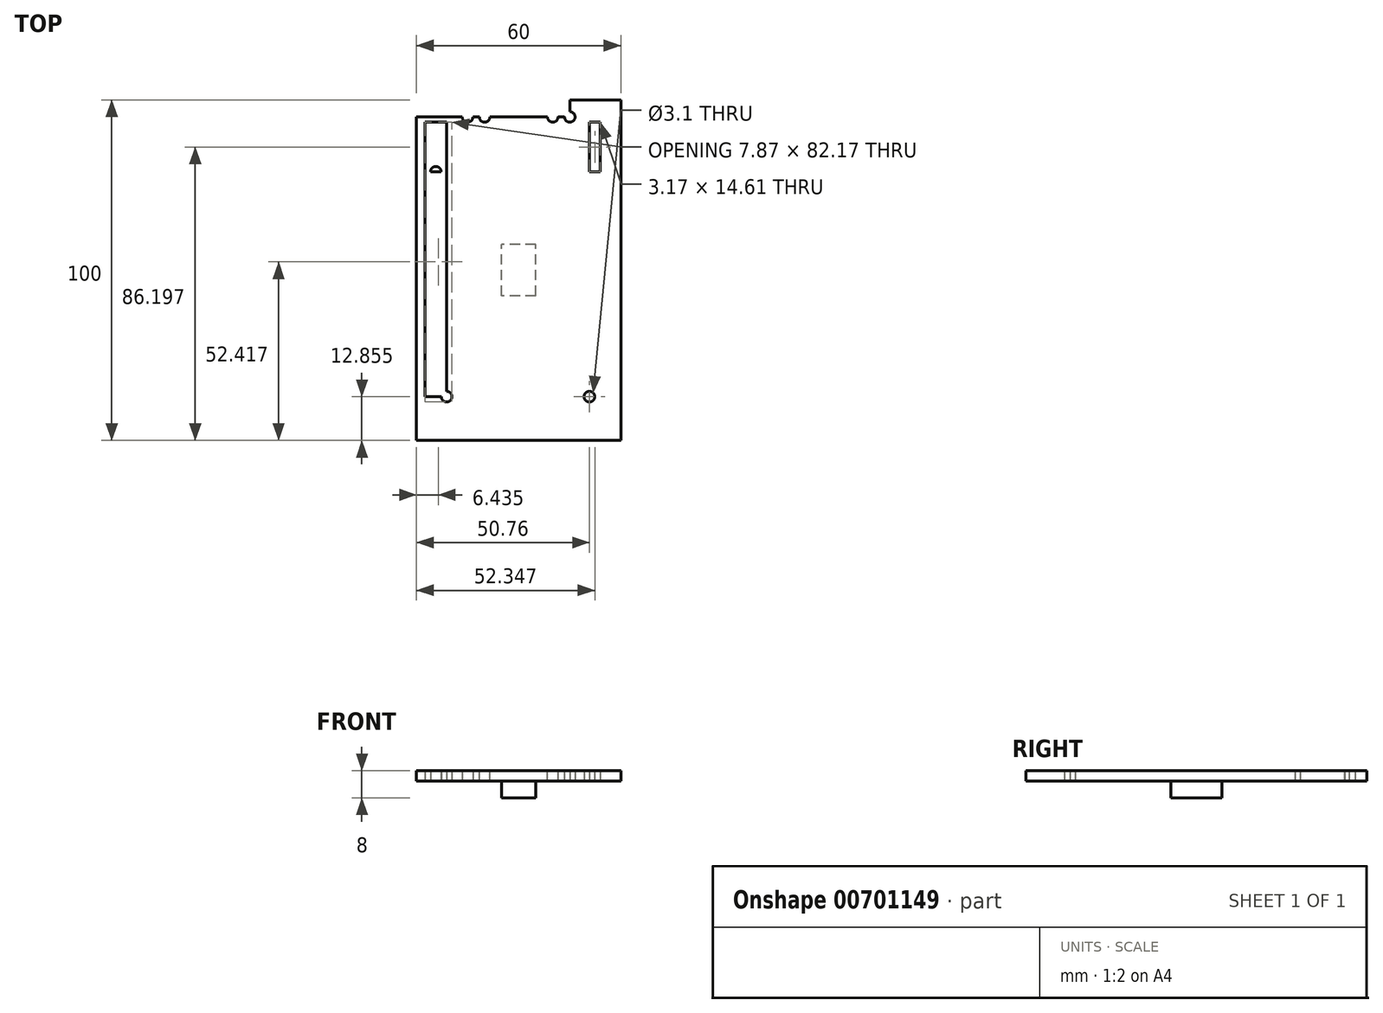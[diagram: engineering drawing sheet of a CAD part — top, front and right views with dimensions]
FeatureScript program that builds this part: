
annotation { "Feature Type Name" : "Feature", "Feature Type Description" : "" }
export const myFeature = defineFeature(function(context is Context, id is Id, definition is map)
    precondition{}
    {
        {
            var Q0;
            Q0=qCreatedBy(makeId("Top.planeOp"),FACE);
            var sketch = newSketch(context, id + "F0", { "sketchPlane" : qUnion([Q0])});
            skLineSegment(sketch, "E0.bottom", {"start": v(30, -50) * mm, "end": v(-30, -50) * mm});
            skLineSegment(sketch, "E0.top", {"start": v(30, 50) * mm, "end": v(-30, 50) * mm});
            skLineSegment(sketch, "E0.left", {"start": v(30, -50) * mm, "end": v(30, 50) * mm});
            skLineSegment(sketch, "E0.right", {"start": v(-30, -50) * mm, "end": v(-30, 50) * mm});
            skPoint(sketch, "E0.middle", {"position": v(0, 0) * mm});
            skLineSegment(sketch, "E1.bottom", {"start": v(-30, 50) * mm, "end": v(-15, 50) * mm});
            skLineSegment(sketch, "E1.top", {"start": v(-30, 45) * mm, "end": v(-15, 45) * mm});
            skLineSegment(sketch, "E1.left", {"start": v(-30, 50) * mm, "end": v(-30, 45) * mm});
            skLineSegment(sketch, "E1.right", {"start": v(-15, 50) * mm, "end": v(-15, 45) * mm});
            skLineSegment(sketch, "E2.bottom", {"start": v(-15, 50) * mm, "end": v(15, 50) * mm});
            skLineSegment(sketch, "E2.top", {"start": v(-15, 45) * mm, "end": v(15, 45) * mm});
            skLineSegment(sketch, "E2.right", {"start": v(15, 50) * mm, "end": v(15, 45) * mm});
            skCircle(sketch, "E3", {"center": v(-15, 45) * mm, "radius": 1.55 * mm});
            skCircle(sketch, "E4", {"center": v(15, 45) * mm, "radius": 1.55 * mm});
            skLineSegment(sketch, "E5.bottom", {"start": v(5, -7.5) * mm, "end": v(-5, -7.5) * mm});
            skLineSegment(sketch, "E5.top", {"start": v(5, 7.5) * mm, "end": v(-5, 7.5) * mm});
            skLineSegment(sketch, "E5.left", {"start": v(5, -7.5) * mm, "end": v(5, 7.5) * mm});
            skLineSegment(sketch, "E5.right", {"start": v(-5, -7.5) * mm, "end": v(-5, 7.5) * mm});
            skLineSegment(sketch, "E6.bottom", {"start": v(27.5, -43.5) * mm, "end": v(-27.5, -43.5) * mm});
            skLineSegment(sketch, "E6.top", {"start": v(27.5, 43.5) * mm, "end": v(-27.5, 43.5) * mm});
            skLineSegment(sketch, "E6.left", {"start": v(27.5, -43.5) * mm, "end": v(27.5, 43.5) * mm});
            skLineSegment(sketch, "E6.right", {"start": v(-27.5, -43.5) * mm, "end": v(-27.5, 43.5) * mm});
            skLineSegment(sketch, "E7.bottom", {"start": v(-27.5, 43.5) * mm, "end": v(-24.33, 43.5) * mm});
            skLineSegment(sketch, "E7.top", {"start": v(-27.5, 28.9) * mm, "end": v(-24.33, 28.9) * mm});
            skLineSegment(sketch, "E7.left", {"start": v(-27.5, 43.5) * mm, "end": v(-27.5, 28.9) * mm});
            skLineSegment(sketch, "E7.right", {"start": v(-24.33, 43.5) * mm, "end": v(-24.33, 28.9) * mm});
            skLineSegment(sketch, "E8.bottom", {"start": v(-27.5, 43.5) * mm, "end": v(23.93, 43.5) * mm});
            skLineSegment(sketch, "E8.top", {"start": v(-27.5, 28.9) * mm, "end": v(23.93, 28.9) * mm});
            skLineSegment(sketch, "E8.right", {"start": v(23.93, 43.5) * mm, "end": v(23.93, 28.9) * mm});
            skCircle(sketch, "E9", {"center": v(-24.33, 28.9) * mm, "radius": 1.55 * mm});
            skCircle(sketch, "E10", {"center": v(23.93, 28.9) * mm, "radius": 1.55 * mm});
            skLineSegment(sketch, "E11.bottom", {"start": v(-27.5, 43.5) * mm, "end": v(-21.15, 43.5) * mm});
            skLineSegment(sketch, "E11.top", {"start": v(-27.5, -37.14) * mm, "end": v(-21.15, -37.14) * mm});
            skLineSegment(sketch, "E11.left", {"start": v(-27.5, 43.5) * mm, "end": v(-27.5, -37.14) * mm});
            skLineSegment(sketch, "E11.right", {"start": v(-21.15, 43.5) * mm, "end": v(-21.15, -37.15) * mm});
            skLineSegment(sketch, "E12.bottom", {"start": v(-27.5, 43.5) * mm, "end": v(20.76, 43.5) * mm});
            skLineSegment(sketch, "E12.top", {"start": v(-27.5, -37.14) * mm, "end": v(20.76, -37.14) * mm});
            skLineSegment(sketch, "E12.right", {"start": v(20.76, 43.5) * mm, "end": v(20.76, -37.14) * mm});
            skCircle(sketch, "E13", {"center": v(-21.15, -37.14) * mm, "radius": 1.55 * mm});
            skCircle(sketch, "E14", {"center": v(20.76, -37.14) * mm, "radius": 1.55 * mm});
            skSolve(sketch);
        }
        {
            var Q0;
            Q0=makeQuery(id+"F0.imprint","IMPRINT",FACE,{"disambiguationData":[TD([[makeQuery(id+"F0.imprint","IMPRINT",EDGE,{"derivedFrom":sQuery(id+"F0.wireOp",EDGE,"E5.bottom")}),-1.0]])]});
            extrude(context, id + "F1", {"entities" : qUnion([Q0]), "oppositeDirection" : true, "depth" : 5 * mm, "offsetDistance" : 25 * mm});
        }
        {
            var Q0;
            Q0=makeQuery(id+"F0.imprint","IMPRINT",FACE,{"disambiguationData":[TD([[makeQuery(id+"F0.imprint","IMPRINT",EDGE,{"derivedFrom":sQuery(id+"F0.wireOp",EDGE,"E5.bottom")}),1.0]])]});
            var Q1;
            Q1=makeQuery(id+"F0.imprint","IMPRINT",FACE,{"disambiguationData":[TD([[makeQuery(id+"F0.imprint","IMPRINT",EDGE,{"derivedFrom":sQuery(id+"F0.wireOp",EDGE,"E5.bottom")}),-1.0]])]});
            var Q2;
            {var subQ1=sQuery(id+"F0.wireOp",EDGE,"E8.top");var subQ4=sQuery(id+"F0.wireOp",EDGE,"E11.left");var subQ5=makeQuery(id+"F0.imprint","INTERSECT",VERTEX,{"derivedFrom":[subQ1,subQ4]});Q2=makeQuery(id+"F0.imprint","IMPRINT",FACE,{"disambiguationData":[TD([[makeQuery(id+"F0.imprint","IMPRINT",EDGE,{"disambiguationData":[TD([[subQ5,-1.0]])],"derivedFrom":subQ1}),-1.0]])]});}
            var Q3;
            Q3=makeQuery(id+"F0.imprint","IMPRINT",FACE,{"disambiguationData":[TD([[makeQuery(id+"F0.imprint","IMPRINT",EDGE,{"derivedFrom":sQuery(id+"F0.wireOp",EDGE,"E0.bottom")}),-1.0]])]});
            var Q4;
            Q4=makeQuery(id+"F0.imprint","IMPRINT",FACE,{"disambiguationData":[TD([[makeQuery(id+"F0.imprint","IMPRINT",EDGE,{"derivedFrom":sQuery(id+"F0.wireOp",EDGE,"E6.bottom")}),-1.0]])]});
            var Q5;
            {var subQ1=sQuery(id+"F0.wireOp",EDGE,"E7.right");var subQ7=sQuery(id+"F0.wireOp",EDGE,"E12.bottom");var subQ8=makeQuery(id+"F0.imprint","INTERSECT",VERTEX,{"derivedFrom":[subQ1,subQ7]});Q5=makeQuery(id+"F0.imprint","IMPRINT",FACE,{"disambiguationData":[TD([[makeQuery(id+"F0.imprint","IMPRINT",EDGE,{"disambiguationData":[TD([[subQ8,-1.0]])],"derivedFrom":subQ1}),-1.0]])]});}
            var Q6;
            {var subQ0=sQuery(id+"F0.wireOp",EDGE,"E12.bottom");var subQ7=sQuery(id+"F0.wireOp",EDGE,"E7.right");var subQ9=makeQuery(id+"F0.imprint","INTERSECT",VERTEX,{"derivedFrom":[subQ7,subQ0]});Q6=makeQuery(id+"F0.imprint","IMPRINT",FACE,{"disambiguationData":[TD([[makeQuery(id+"F0.imprint","IMPRINT",EDGE,{"disambiguationData":[TD([[subQ9,-1.0]])],"derivedFrom":subQ7}),1.0]])]});}
            var Q7;
            {var subQ0=sQuery(id+"F0.wireOp",EDGE,"E12.bottom");var subQ11=sQuery(id+"F0.wireOp",EDGE,"E3");var subQ12=makeQuery(id+"F0.imprint","INTERSECT",VERTEX,{"disambiguationData":[OD(0.0)],"derivedFrom":[subQ11,subQ0]});Q7=makeQuery(id+"F0.imprint","IMPRINT",FACE,{"disambiguationData":[TD([[makeQuery(id+"F0.imprint","IMPRINT",EDGE,{"disambiguationData":[TD([[subQ12,-1.0]])],"derivedFrom":subQ11}),-1.0]])]});}
            var Q8;
            {var subQ5=sQuery(id+"F0.wireOp",EDGE,"E8.bottom");Q8=makeQuery(id+"F0.imprint","IMPRINT",FACE,{"disambiguationData":[TD([[makeQuery(id+"F0.imprint","IMPRINT",EDGE,{"derivedFrom":subQ5}),-1.0]])]});}
            var Q9;
            {var subQ1=sQuery(id+"F0.wireOp",EDGE,"E2.bottom");Q9=makeQuery(id+"F0.imprint","IMPRINT",FACE,{"disambiguationData":[TD([[makeQuery(id+"F0.imprint","IMPRINT",EDGE,{"derivedFrom":subQ1}),-1.0]])]});}
            var Q10;
            {var subQ1=sQuery(id+"F0.wireOp",EDGE,"E1.bottom");Q10=makeQuery(id+"F0.imprint","IMPRINT",FACE,{"disambiguationData":[TD([[makeQuery(id+"F0.imprint","IMPRINT",EDGE,{"derivedFrom":subQ1}),-1.0]])]});}
            var Q11;
            {var subQ0=sQuery(id+"F0.wireOp",EDGE,"E3");var subQ1=sQuery(id+"F0.wireOp",EDGE,"E2.top");var subQ2=makeQuery(id+"F0.imprint","INTERSECT",VERTEX,{"derivedFrom":[subQ1,subQ0]});Q11=makeQuery(id+"F0.imprint","IMPRINT",FACE,{"disambiguationData":[TD([[makeQuery(id+"F0.imprint","IMPRINT",EDGE,{"disambiguationData":[TD([[subQ2,-1.0]])],"derivedFrom":subQ1}),-1.0]])]});}
            extrude(context, id + "F2", {"entities" : qUnion([Q0, Q1, Q2, Q3, Q4, Q5, Q6, Q7, Q8, Q9, Q10, Q11]), "operationType" : NewBodyOperationType.ADD, "depth" : 3 * mm, "offsetDistance" : 25 * mm});
        }
        {
            var Q0;
            Q0=makeQuery(id+"F2.opExtrude","CAP_FACE",FACE,{"disambiguationData":[OSD([sQuery(id+"F0.wireOp",EDGE,"E0.bottom"),sQuery(id+"F0.wireOp",EDGE,"E0.top"),sQuery(id+"F0.wireOp",EDGE,"E0.left"),sQuery(id+"F0.wireOp",EDGE,"E0.right"),sQuery(id+"F0.wireOp",EDGE,"E1.bottom"),sQuery(id+"F0.wireOp",EDGE,"E1.left"),sQuery(id+"F0.wireOp",EDGE,"E2.bottom"),sQuery(id+"F0.wireOp",EDGE,"E3"),sQuery(id+"F0.wireOp",EDGE,"E4"),sQuery(id+"F0.wireOp",EDGE,"E9"),sQuery(id+"F0.wireOp",EDGE,"E10"),sQuery(id+"F0.wireOp",EDGE,"E13"),sQuery(id+"F0.wireOp",EDGE,"E14")])],"isStart":false});
            var sketch = newSketch(context, id + "F3", { "sketchPlane" : qUnion([Q0])});
            skLineSegment(sketch, "E15.bottom", {"start": v(-30, 50) * mm, "end": v(30, 50) * mm});
            skLineSegment(sketch, "E15.top", {"start": v(-30, 45) * mm, "end": v(30, 45) * mm});
            skLineSegment(sketch, "E15.left", {"start": v(-30, 50) * mm, "end": v(-30, 45) * mm});
            skLineSegment(sketch, "E15.right", {"start": v(30, 50) * mm, "end": v(30, 45) * mm});
            skLineSegment(sketch, "E16.top", {"start": v(-30, 40) * mm, "end": v(30, 40) * mm});
            skLineSegment(sketch, "E16.left", {"start": v(-30, 45) * mm, "end": v(-30, 40) * mm});
            skLineSegment(sketch, "E16.right", {"start": v(30, 45) * mm, "end": v(30, 40) * mm});
            skLineSegment(sketch, "E17.bottom", {"start": v(-30, 50) * mm, "end": v(-10, 50) * mm});
            skLineSegment(sketch, "E17.top", {"start": v(-30, 45) * mm, "end": v(-10, 45) * mm});
            skLineSegment(sketch, "E17.right", {"start": v(-10, 50) * mm, "end": v(-10, 45) * mm});
            skLineSegment(sketch, "E18.bottom", {"start": v(30, 50) * mm, "end": v(10, 50) * mm});
            skLineSegment(sketch, "E18.top", {"start": v(30, 45) * mm, "end": v(10, 45) * mm});
            skLineSegment(sketch, "E18.right", {"start": v(10, 50) * mm, "end": v(10, 45) * mm});
            skCircle(sketch, "E19", {"center": v(-10, 45) * mm, "radius": 1.55 * mm});
            skCircle(sketch, "E20", {"center": v(10, 45) * mm, "radius": 1.55 * mm});
            skSolve(sketch);
        }
        {
            var Q0;
            {var subQ1=sQuery(id+"F3.wireOp",EDGE,"E15.bottom");Q0=makeQuery(id+"F3.imprint","IMPRINT",FACE,{"disambiguationData":[TD([[makeQuery(id+"F3.imprint","IMPRINT",EDGE,{"derivedFrom":subQ1}),1.0]])]});}
            var Q1;
            {var subQ7=sQuery(id+"F3.wireOp",EDGE,"E18.bottom");Q1=makeQuery(id+"F3.imprint","IMPRINT",FACE,{"disambiguationData":[TD([[makeQuery(id+"F3.imprint","IMPRINT",EDGE,{"derivedFrom":subQ7}),1.0]])]});}
            var Q2;
            Q2=makeQuery(id+"F3.imprint","IMPRINT",FACE,{"disambiguationData":[TD([[makeQuery(id+"F3.imprint","IMPRINT",EDGE,{"derivedFrom":sQuery(id+"F3.wireOp",EDGE,"E16.top")}),1.0]])]});
            var Q3;
            {var subQ0=sQuery(id+"F3.wireOp",EDGE,"E17.top");var subQ1=makeQuery(id+"F2.opExtrude","CAP_EDGE",EDGE,{"disambiguationData":[OSD([sQuery(id+"F0.wireOp",EDGE,"E3")])],"isStart":false});var subQ2=makeQuery(id+"F3.imprint","INTERSECT",VERTEX,{"disambiguationData":[OD(0.0)],"derivedFrom":[subQ1,subQ0]});Q3=makeQuery(id+"F3.imprint","IMPRINT",FACE,{"disambiguationData":[TD([[makeQuery(id+"F3.imprint","IMPRINT",EDGE,{"disambiguationData":[TD([[subQ2,-1.0]])],"derivedFrom":subQ0}),-1.0]])]});}
            var Q4;
            {var subQ0=sQuery(id+"F3.wireOp",EDGE,"E17.top");var subQ1=makeQuery(id+"F2.opExtrude","CAP_EDGE",EDGE,{"disambiguationData":[OSD([sQuery(id+"F0.wireOp",EDGE,"E3")])],"isStart":false});var subQ2=makeQuery(id+"F3.imprint","INTERSECT",VERTEX,{"disambiguationData":[OD(0.0)],"derivedFrom":[subQ1,subQ0]});Q4=makeQuery(id+"F3.imprint","IMPRINT",FACE,{"disambiguationData":[TD([[makeQuery(id+"F3.imprint","IMPRINT",EDGE,{"disambiguationData":[TD([[subQ2,-1.0]])],"derivedFrom":subQ0}),1.0]])]});}
            var Q5;
            {var subQ7=sQuery(id+"F3.wireOp",EDGE,"E17.bottom");Q5=makeQuery(id+"F3.imprint","IMPRINT",FACE,{"disambiguationData":[TD([[makeQuery(id+"F3.imprint","IMPRINT",EDGE,{"derivedFrom":subQ7}),1.0]])]});}
            var Q6;
            {var subQ0=sQuery(id+"F3.wireOp",EDGE,"E18.top");var subQ1=makeQuery(id+"F2.opExtrude","CAP_EDGE",EDGE,{"disambiguationData":[OSD([sQuery(id+"F0.wireOp",EDGE,"E4")])],"isStart":false});var subQ2=makeQuery(id+"F3.imprint","INTERSECT",VERTEX,{"disambiguationData":[OD(0.0)],"derivedFrom":[subQ1,subQ0]});Q6=makeQuery(id+"F3.imprint","IMPRINT",FACE,{"disambiguationData":[TD([[makeQuery(id+"F3.imprint","IMPRINT",EDGE,{"disambiguationData":[TD([[subQ2,-1.0]])],"derivedFrom":subQ0}),1.0]])]});}
            var Q7;
            {var subQ0=sQuery(id+"F3.wireOp",EDGE,"E18.top");var subQ1=makeQuery(id+"F2.opExtrude","CAP_EDGE",EDGE,{"disambiguationData":[OSD([sQuery(id+"F0.wireOp",EDGE,"E4")])],"isStart":false});var subQ2=makeQuery(id+"F3.imprint","INTERSECT",VERTEX,{"disambiguationData":[OD(0.0)],"derivedFrom":[subQ1,subQ0]});Q7=makeQuery(id+"F3.imprint","IMPRINT",FACE,{"disambiguationData":[TD([[makeQuery(id+"F3.imprint","IMPRINT",EDGE,{"disambiguationData":[TD([[subQ2,-1.0]])],"derivedFrom":subQ0}),-1.0]])]});}
            extrude(context, id + "F4", {"entities" : qUnion([Q0, Q1, Q2, Q3, Q4, Q5, Q6, Q7]), "operationType" : NewBodyOperationType.ADD, "oppositeDirection" : true, "depth" : 3 * mm, "offsetDistance" : 25 * mm});
        }
        {
            var Q0;
            {var subQ1=sQuery(id+"F3.wireOp",EDGE,"E15.top");var subQ3=sQuery(id+"F3.wireOp",EDGE,"E19");var subQ4=makeQuery(id+"F3.imprint","INTERSECT",VERTEX,{"derivedFrom":[subQ1,subQ3]});Q0=makeQuery(id+"F3.imprint","IMPRINT",FACE,{"disambiguationData":[TD([[makeQuery(id+"F3.imprint","IMPRINT",EDGE,{"disambiguationData":[TD([[subQ4,1.0]])],"derivedFrom":subQ3}),1.0]])]});}
            var Q1;
            {var subQ1=sQuery(id+"F3.wireOp",EDGE,"E15.top");var subQ3=sQuery(id+"F3.wireOp",EDGE,"E19");var subQ4=makeQuery(id+"F3.imprint","INTERSECT",VERTEX,{"derivedFrom":[subQ1,subQ3]});Q1=makeQuery(id+"F3.imprint","IMPRINT",FACE,{"disambiguationData":[TD([[makeQuery(id+"F3.imprint","IMPRINT",EDGE,{"disambiguationData":[TD([[subQ4,-1.0]])],"derivedFrom":subQ3}),1.0]])]});}
            var Q2;
            {var subQ1=sQuery(id+"F3.wireOp",EDGE,"E17.top");var subQ3=sQuery(id+"F3.wireOp",EDGE,"E19");var subQ4=makeQuery(id+"F3.imprint","INTERSECT",VERTEX,{"derivedFrom":[subQ1,subQ3]});Q2=makeQuery(id+"F3.imprint","IMPRINT",FACE,{"disambiguationData":[TD([[makeQuery(id+"F3.imprint","IMPRINT",EDGE,{"disambiguationData":[TD([[subQ4,1.0]])],"derivedFrom":subQ3}),1.0]])]});}
            var Q3;
            {var subQ1=sQuery(id+"F3.wireOp",EDGE,"E18.top");var subQ3=sQuery(id+"F3.wireOp",EDGE,"E20");var subQ4=makeQuery(id+"F3.imprint","INTERSECT",VERTEX,{"derivedFrom":[subQ1,subQ3]});Q3=makeQuery(id+"F3.imprint","IMPRINT",FACE,{"disambiguationData":[TD([[makeQuery(id+"F3.imprint","IMPRINT",EDGE,{"disambiguationData":[TD([[subQ4,-1.0]])],"derivedFrom":subQ3}),1.0]])]});}
            var Q4;
            {var subQ1=sQuery(id+"F3.wireOp",EDGE,"E15.top");var subQ3=sQuery(id+"F3.wireOp",EDGE,"E20");var subQ4=makeQuery(id+"F3.imprint","INTERSECT",VERTEX,{"derivedFrom":[subQ1,subQ3]});Q4=makeQuery(id+"F3.imprint","IMPRINT",FACE,{"disambiguationData":[TD([[makeQuery(id+"F3.imprint","IMPRINT",EDGE,{"disambiguationData":[TD([[subQ4,1.0]])],"derivedFrom":subQ3}),1.0]])]});}
            var Q5;
            {var subQ1=sQuery(id+"F3.wireOp",EDGE,"E15.top");var subQ3=sQuery(id+"F3.wireOp",EDGE,"E20");var subQ4=makeQuery(id+"F3.imprint","INTERSECT",VERTEX,{"derivedFrom":[subQ1,subQ3]});Q5=makeQuery(id+"F3.imprint","IMPRINT",FACE,{"disambiguationData":[TD([[makeQuery(id+"F3.imprint","IMPRINT",EDGE,{"disambiguationData":[TD([[subQ4,-1.0]])],"derivedFrom":subQ3}),1.0]])]});}
            extrude(context, id + "F5", {"entities" : qUnion([Q0, Q1, Q2, Q3, Q4, Q5]), "operationType" : NewBodyOperationType.REMOVE, "oppositeDirection" : true, "depth" : 25 * mm, "offsetDistance" : 25 * mm});
        }
    });
